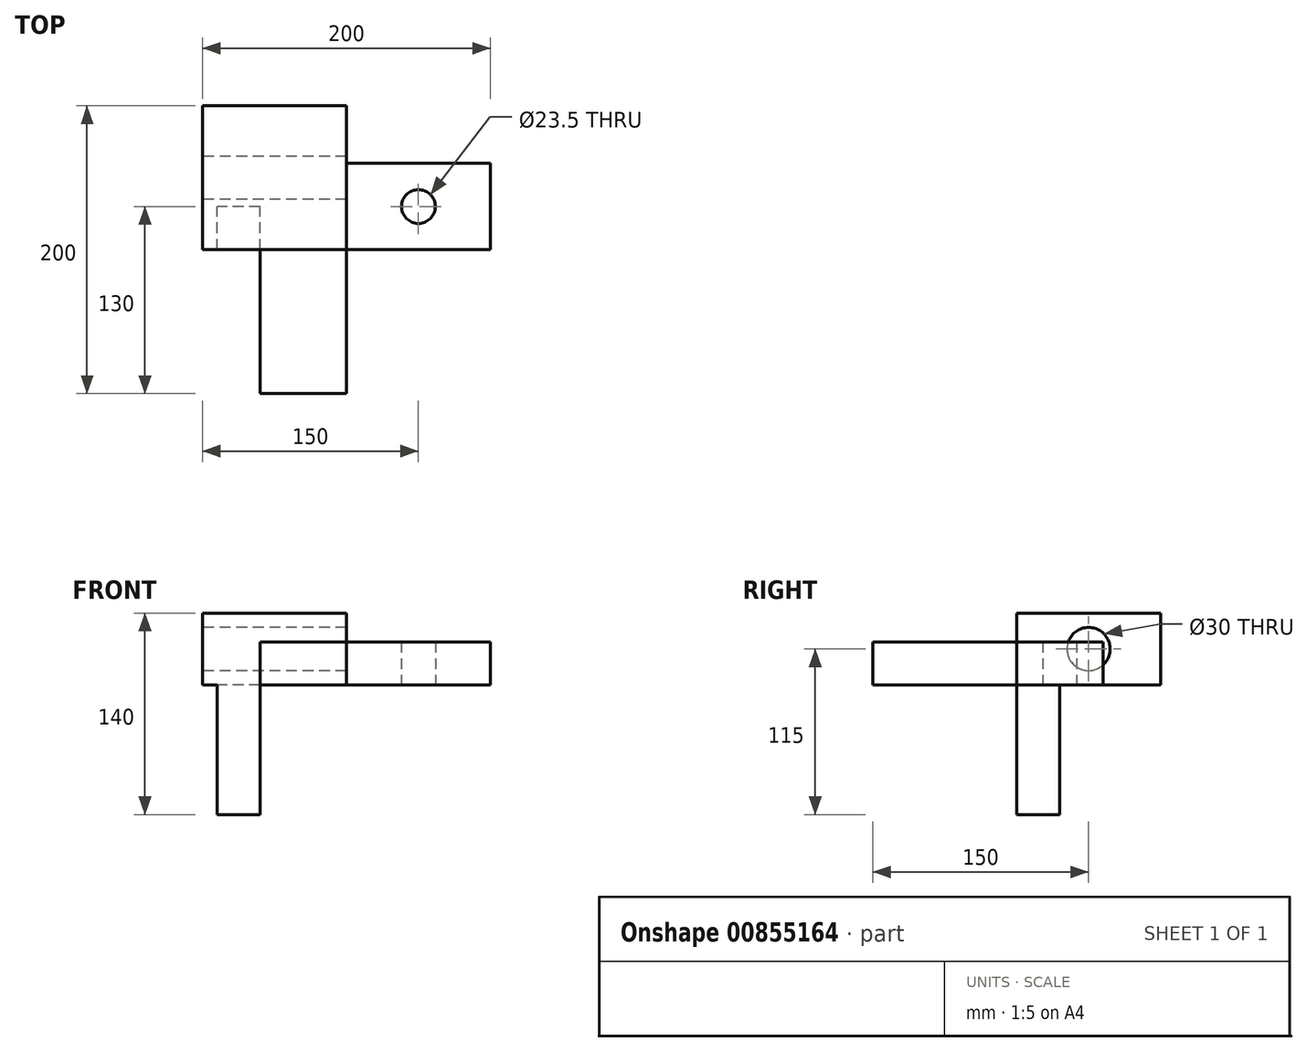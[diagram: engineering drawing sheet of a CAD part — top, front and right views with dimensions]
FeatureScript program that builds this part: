
annotation { "Feature Type Name" : "Feature", "Feature Type Description" : "" }
export const myFeature = defineFeature(function(context is Context, id is Id, definition is map)
    precondition{}
    {
        {
            var Q0;
            Q0=qCreatedBy(makeId("Top.planeOp"),FACE);
            var sketch = newSketch(context, id + "F0", { "sketchPlane" : qUnion([Q0])});
            skLineSegment(sketch, "E0.bottom", {"start": v(0, 0) * mm, "end": v(100, 0) * mm});
            skLineSegment(sketch, "E0.top", {"start": v(0, 60) * mm, "end": v(100, 60) * mm});
            skLineSegment(sketch, "E0.left", {"start": v(0, 0) * mm, "end": v(0, 60) * mm});
            skLineSegment(sketch, "E0.right", {"start": v(100, 0) * mm, "end": v(100, 60) * mm});
            skCircle(sketch, "E1", {"center": v(50, 30) * mm, "radius": 11.75 * mm});
            skPoint(sketch, "E1.centerSnap0", {"position": v(0, 30) * mm});
            skPoint(sketch, "E1.centerSnap1", {"position": v(50, 60) * mm});
            skSolve(sketch);
        }
        {
            var Q0;
            Q0=makeQuery(id+"F0.imprint","IMPRINT",FACE,{"disambiguationData":[TD([[makeQuery(id+"F0.imprint","IMPRINT",EDGE,{"derivedFrom":sQuery(id+"F0.wireOp",EDGE,"E0.bottom")}),1.0]])]});
            extrude(context, id + "F1", {"entities" : qUnion([Q0]), "depth" : 30 * mm, "offsetDistance" : 25 * mm});
        }
        {
            var Q0;
            Q0=qCreatedBy(makeId("Top.planeOp"),FACE);
            var sketch = newSketch(context, id + "F2", { "sketchPlane" : qUnion([Q0])});
            skLineSegment(sketch, "E2.bottom", {"start": v(0, 0) * mm, "end": v(-60, 0) * mm});
            skLineSegment(sketch, "E2.top", {"start": v(0, -100) * mm, "end": v(-60, -100) * mm});
            skLineSegment(sketch, "E2.left", {"start": v(0, 0) * mm, "end": v(0, -100) * mm});
            skLineSegment(sketch, "E2.right", {"start": v(-60, 0) * mm, "end": v(-60, -100) * mm});
            skLineSegment(sketch, "E3.bottom", {"start": v(-60, 0) * mm, "end": v(-90, 0) * mm});
            skLineSegment(sketch, "E3.top", {"start": v(-60, 30) * mm, "end": v(-90, 30) * mm});
            skLineSegment(sketch, "E3.left", {"start": v(-60, 0) * mm, "end": v(-60, 30) * mm});
            skLineSegment(sketch, "E3.right", {"start": v(-90, 0) * mm, "end": v(-90, 30) * mm});
            skSolve(sketch);
        }
        {
            var Q0;
            Q0=makeQuery(id+"F2.imprint","IMPRINT",FACE,{"disambiguationData":[TD([[makeQuery(id+"F2.imprint","IMPRINT",EDGE,{"derivedFrom":sQuery(id+"F2.wireOp",EDGE,"E2.bottom")}),1.0]])]});
            extrude(context, id + "F3", {"entities" : qUnion([Q0]), "depth" : 30 * mm, "offsetDistance" : 25 * mm});
        }
        {
            var Q0;
            Q0=qCreatedBy(makeId("Top.planeOp"),FACE);
            var sketch = newSketch(context, id + "F4", { "sketchPlane" : qUnion([Q0])});
            skLineSegment(sketch, "E4.bottom", {"start": v(0, 0) * mm, "end": v(-100, 0) * mm});
            skLineSegment(sketch, "E4.top", {"start": v(0, 100) * mm, "end": v(-100, 100) * mm});
            skLineSegment(sketch, "E4.left", {"start": v(0, 0) * mm, "end": v(0, 100) * mm});
            skLineSegment(sketch, "E4.right", {"start": v(-100, 0) * mm, "end": v(-100, 100) * mm});
            skSolve(sketch);
        }
        {
            var Q0;
            Q0=makeQuery(id+"F4.imprint","IMPRINT",FACE,{"disambiguationData":[TD([[makeQuery(id+"F4.imprint","IMPRINT",EDGE,{"derivedFrom":sQuery(id+"F4.wireOp",EDGE,"E4.bottom")}),-1.0]])]});
            extrude(context, id + "F5", {"entities" : qUnion([Q0]), "depth" : 50 * mm, "offsetDistance" : 25 * mm});
        }
        {
            var Q0;
            Q0=makeQuery(id+"F5.opExtrude","SWEPT_FACE",FACE,{"disambiguationData":[OSD([sQuery(id+"F4.wireOp",EDGE,"E4.right")])]});
            var sketch = newSketch(context, id + "F6", { "sketchPlane" : qUnion([Q0])});
            skCircle(sketch, "E5", {"center": v(-50, 25) * mm, "radius": 15 * mm});
            skPoint(sketch, "E5.centerSnap0", {"position": v(0, 25) * mm});
            skPoint(sketch, "E5.centerSnap1", {"position": v(-50, 50) * mm});
            skSolve(sketch);
        }
        {
            var Q0;
            Q0=makeQuery(id+"F6.imprint","IMPRINT",FACE,{"disambiguationData":[TD([[makeQuery(id+"F6.imprint","IMPRINT",EDGE,{"derivedFrom":sQuery(id+"F6.wireOp",EDGE,"E5")}),1.0]])]});
            extrude(context, id + "F7", {"entities" : qUnion([Q0]), "operationType" : NewBodyOperationType.REMOVE, "endBound" : BoundingType.UP_TO_NEXT, "oppositeDirection" : true, "depth" : 25 * mm, "offsetDistance" : 25 * mm});
        }
        {
            var Q0;
            Q0=makeQuery(id+"F2.imprint","IMPRINT",FACE,{"disambiguationData":[TD([[makeQuery(id+"F2.imprint","IMPRINT",EDGE,{"derivedFrom":sQuery(id+"F2.wireOp",EDGE,"E3.bottom")}),-1.0]])]});
            extrude(context, id + "F8", {"entities" : qUnion([Q0]), "operationType" : NewBodyOperationType.ADD, "oppositeDirection" : true, "depth" : 90 * mm, "offsetDistance" : 25 * mm});
        }
    });
